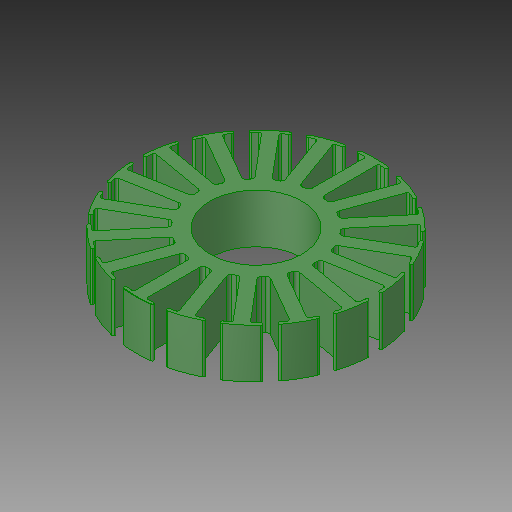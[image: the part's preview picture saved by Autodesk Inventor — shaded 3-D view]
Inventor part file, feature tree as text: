
AUTODESK INVENTOR PART (.ipt)
format: ipt  version: 2019.4 (Build 234330000, 330)  size: 399,360 bytes
history: mixed  units: mm
features: fillet x1, imported_body x1
ambient origin geometry x8: Origin, YZ Plane, XZ Plane, XY Plane, X Axis, Y Axis, Z Axis, Center Point
bodies: Solid1 (imported_parasolid)
feature tree (2):
  fillet  "Fillet3"  [1 undecoded]
  imported_body  NMx_Import_Brep_tag  [imported B-rep: ~38 faces, bbox_mm=[19.916905, 8.0, 37.914944]]
note: 1 required parameter value undecoded (feature->parameter linkage not recoverable at this tier; creation-order binding heuristic only, values carry confidence <= 0.55)
